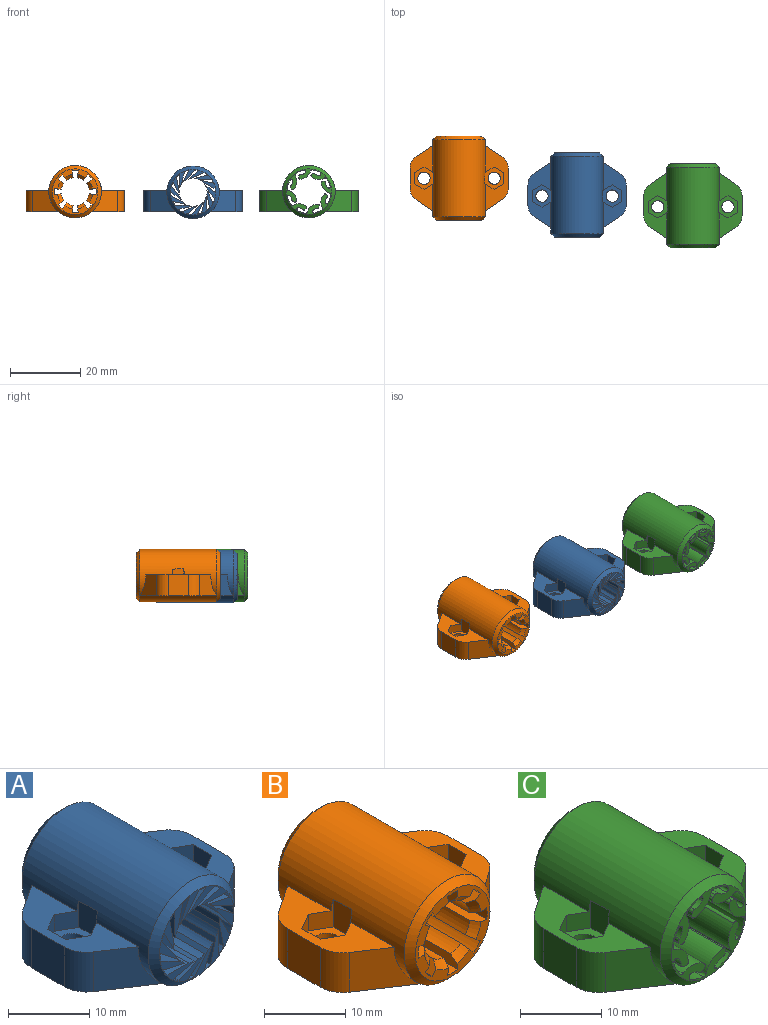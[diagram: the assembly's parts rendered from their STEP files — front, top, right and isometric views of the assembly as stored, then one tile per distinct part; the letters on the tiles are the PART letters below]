
ASSEMBLY  parts=3 mates=2
PART A: 91 faces, bbox 28x24x15 mm
  f0: plane 18.59x6.51mm, normal (0,0,1), area 66.2mm2, adj f1,f2,f4,f5,f6,f7,f82,f83
  f1: cylinder r=7.5mm len=22mm, axis (0,1,0), area 762.8mm2, adj f0,f3,f4,f5,f66,f67,f68,f69
  f2: plane 6x5.69mm, normal (-1,0,0), area 34.2mm2, adj f0,f3,f6,f7
  f3: plane 21.87x9mm, normal (0,0,-1), area 132.4mm2, adj f1,f2,f4,f5,f6,f7,f89
  f4: plane 7.2x6mm, normal (-0.55,-0.83,0), area 38.9mm2, adj f0,f1,f3,f6
  f5: plane 7.2x6mm, normal (-0.55,0.83,0), area 38.9mm2, adj f0,f1,f3,f7
  f6: cylinder r=4mm len=6mm, axis (0,0,-1), area 23.7mm2, adj f0,f2,f3,f4
  f7: cylinder r=4mm len=6mm, axis (0,0,-1), area 23.7mm2, adj f0,f2,f3,f5
  f8: cylinder r=6.35mm len=24mm, axis (0,1,0), area 28.5mm2, adj f9,f63,f64,f65
  f9: plane 24x3.4mm, normal (-0.9,0,-0.44), area 91mm2, adj f8,f10,f64,f65
  f10: cylinder r=4mm len=24mm, axis (0,1,0), area 25.1mm2, adj f9,f11,f64,f65
  f11: plane 24x3.72mm, normal (0.98,0,0.2), area 91mm2, adj f10,f12,f64,f65
  f12: cylinder r=6.35mm len=24mm, axis (0,1,0), area 28.5mm2, adj f11,f13,f64,f65
  f13: plane 24x3.79mm, normal (-1,0,-0.01), area 91mm2, adj f12,f14,f64,f65
  f14: cylinder r=4mm len=24mm, axis (0,1,0), area 25.1mm2, adj f13,f15,f64,f65
  f15: plane 24x3.67mm, normal (0.97,0,-0.25), area 91mm2, adj f14,f16,f64,f65
  f16: cylinder r=6.35mm len=24mm, axis (0,1,0), area 28.5mm2, adj f15,f17,f64,f65
  f17: plane 24x3.44mm, normal (-0.91,0,0.42), area 91mm2, adj f16,f18,f64,f65
  f18: cylinder r=4mm len=24mm, axis (0,1,0), area 25.1mm2, adj f17,f19,f64,f65
  f19: plane 24x2.9mm, normal (0.77,0,-0.64), area 91mm2, adj f18,f20,f64,f65
  f20: cylinder r=6.35mm len=24mm, axis (0,1,0), area 28.5mm2, adj f19,f21,f64,f65
  f21: plane 24x2.94mm, normal (-0.63,0,0.77), area 91mm2, adj f20,f22,f64,f65
  f22: cylinder r=4mm len=24mm, axis (0,1,0), area 25.1mm2, adj f21,f23,f64,f65
  f23: plane 24x3.46mm, normal (0.41,0,-0.91), area 91mm2, adj f22,f24,f64,f65
  f24: cylinder r=6.35mm len=24mm, axis (0,1,0), area 28.5mm2, adj f23,f25,f64,f65
  f25: plane 24x3.69mm, normal (-0.23,0,0.97), area 91mm2, adj f24,f26,f64,f65
  f26: cylinder r=4mm len=24mm, axis (0,1,0), area 25.1mm2, adj f25,f27,f64,f65
  f27: plane 24x3.79mm, normal (-0.03,0,-1), area 91mm2, adj f26,f28,f64,f65
  f28: cylinder r=6.35mm len=24mm, axis (0,1,0), area 28.5mm2, adj f27,f29,f64,f65
  f29: plane 24x3.71mm, normal (0.21,0,0.98), area 91mm2, adj f28,f30,f64,f65
  f30: cylinder r=4mm len=24mm, axis (0,1,0), area 25.1mm2, adj f29,f31,f64,f65
  f31: plane 24x3.37mm, normal (-0.46,0,-0.89), area 91mm2, adj f30,f32,f64,f65
  f32: cylinder r=6.35mm len=24mm, axis (0,1,0), area 28.5mm2, adj f31,f33,f64,f65
  f33: plane 24x2.99mm, normal (0.61,0,0.79), area 91mm2, adj f32,f34,f64,f65
  f34: cylinder r=4mm len=24mm, axis (0,1,0), area 25.1mm2, adj f33,f35,f64,f65
  f35: plane 24x3.02mm, normal (-0.8,0,-0.6), area 91mm2, adj f34,f36,f64,f65
  f36: cylinder r=6.35mm len=24mm, axis (0,1,0), area 28.5mm2, adj f35,f37,f64,f65
  f37: plane 24x3.4mm, normal (0.9,0,0.44), area 91mm2, adj f36,f38,f64,f65
  f38: cylinder r=4mm len=24mm, axis (0,1,0), area 25.1mm2, adj f37,f39,f64,f65
  f39: plane 24x3.72mm, normal (-0.98,0,-0.2), area 91mm2, adj f38,f40,f64,f65
  f40: cylinder r=6.35mm len=24mm, axis (0,1,0), area 28.5mm2, adj f39,f41,f64,f65
  f41: plane 24x3.79mm, normal (1,0,0.01), area 91mm2, adj f40,f42,f64,f65
  f42: cylinder r=4mm len=24mm, axis (0,1,0), area 25.1mm2, adj f41,f43,f64,f65
  f43: plane 24x3.67mm, normal (-0.97,0,0.25), area 91mm2, adj f42,f44,f64,f65
  f44: cylinder r=6.35mm len=24mm, axis (0,1,0), area 28.5mm2, adj f43,f45,f64,f65
  f45: plane 24x3.44mm, normal (0.91,0,-0.42), area 91mm2, adj f44,f46,f64,f65
  f46: cylinder r=4mm len=24mm, axis (0,1,0), area 25.1mm2, adj f45,f47,f64,f65
  f47: plane 24x2.9mm, normal (-0.77,0,0.64), area 91mm2, adj f46,f48,f64,f65
  f48: cylinder r=6.35mm len=24mm, axis (0,1,0), area 28.5mm2, adj f47,f49,f64,f65
  f49: plane 24x2.94mm, normal (0.63,0,-0.77), area 91mm2, adj f48,f50,f64,f65
  f50: cylinder r=4mm len=24mm, axis (0,1,0), area 25.1mm2, adj f49,f51,f64,f65
  f51: plane 24x3.46mm, normal (-0.41,0,0.91), area 91mm2, adj f50,f52,f64,f65
  f52: cylinder r=6.35mm len=24mm, axis (0,1,0), area 28.5mm2, adj f51,f53,f64,f65
  f53: plane 24x3.69mm, normal (0.23,0,-0.97), area 91mm2, adj f52,f54,f64,f65
  f54: cylinder r=4mm len=24mm, axis (0,1,0), area 25.1mm2, adj f53,f55,f64,f65
  f55: plane 24x3.79mm, normal (0.03,0,1), area 91mm2, adj f54,f56,f64,f65
  f56: cylinder r=6.35mm len=24mm, axis (0,1,0), area 28.5mm2, adj f55,f57,f64,f65
  f57: plane 24x3.71mm, normal (-0.21,0,-0.98), area 91mm2, adj f56,f58,f64,f65
  f58: cylinder r=4mm len=24mm, axis (0,1,0), area 25.1mm2, adj f57,f59,f64,f65
  f59: plane 24x3.37mm, normal (0.46,0,0.89), area 91mm2, adj f58,f60,f64,f65
  f60: cylinder r=6.35mm len=24mm, axis (0,1,0), area 28.5mm2, adj f59,f61,f64,f65
  f61: plane 24x2.99mm, normal (-0.61,0,-0.79), area 91mm2, adj f60,f62,f64,f65
  f62: cylinder r=4mm len=24mm, axis (0,1,0), area 25.1mm2, adj f61,f63,f64,f65
  f63: plane 24x3.02mm, normal (0.8,0,0.6), area 91mm2, adj f8,f62,f64,f65
  f64: plane 13x13mm, normal (0,-1,0), area 50.6mm2, adj f8,f9,f10,f11,f12,f13,f14,f15
  f65: plane 13x13mm, normal (0,1,0), area 50.6mm2, adj f8,f9,f10,f11,f12,f13,f14,f15
  f66: cone r=6.5mm half-angle=45deg, axis (0,1,0), area 62.2mm2, adj f1,f64
  f67: cone r=7.5mm half-angle=45deg, axis (0,-1,0), area 62.2mm2, adj f1,f65
  f68: plane 18.59x6.51mm, normal (0,0,1), area 66.2mm2, adj f1,f70,f71,f72,f73,f74,f76,f77
  f69: plane 21.87x9mm, normal (0,0,-1), area 132.4mm2, adj f1,f70,f71,f72,f73,f74,f90
  f70: plane 6x5.69mm, normal (1,0,0), area 34.2mm2, adj f68,f69,f73,f74
  f71: plane 7.2x6mm, normal (0.55,0.83,0), area 38.9mm2, adj f1,f68,f69,f73
  f72: plane 7.2x6mm, normal (0.55,-0.83,0), area 38.9mm2, adj f1,f68,f69,f74
  f73: cylinder r=4mm len=6mm, axis (0,0,1), area 23.7mm2, adj f68,f69,f70,f71
  f74: cylinder r=4mm len=6mm, axis (0,0,1), area 23.7mm2, adj f68,f69,f70,f72
  f75: plane 4.04x3.18mm, normal (1,-0.01,0), area 12.7mm2, adj f1,f76,f77,f81
  f76: plane 4.04x2.74mm, normal (0.5,0.86,0), area 8.2mm2, adj f1,f68,f75,f78,f81
  f77: plane 3.98x2.76mm, normal (0.5,-0.87,0), area 8.2mm2, adj f1,f68,f75,f80,f81
  f78: plane 2.76x2.5mm, normal (-0.5,0.87,0), area 7.9mm2, adj f68,f76,f79,f81
  f79: plane 3.18x2.5mm, normal (-1,0.01,0), area 7.9mm2, adj f68,f78,f80,f81
  f80: plane 2.74x2.5mm, normal (-0.5,-0.86,0), area 7.9mm2, adj f68,f77,f79,f81
  f81: plane 6.35x5.52mm, normal (0,0,1), area 16.6mm2, adj f75,f76,f77,f78,f79,f80,f90
  f82: plane 2.74x2.5mm, normal (0.5,-0.86,0), area 7.9mm2, adj f0,f83,f87,f88
  f83: plane 3.18x2.5mm, normal (1,0.01,0), area 7.9mm2, adj f0,f82,f84,f88
  f84: plane 2.76x2.5mm, normal (0.5,0.87,0), area 7.9mm2, adj f0,f83,f85,f88
  f85: plane 4.04x2.74mm, normal (-0.5,0.86,0), area 8.2mm2, adj f0,f1,f84,f86,f88
  f86: plane 4.04x3.18mm, normal (-1,-0.01,0), area 12.7mm2, adj f1,f85,f87,f88
  f87: plane 3.98x2.76mm, normal (-0.5,-0.87,0), area 8.2mm2, adj f0,f1,f82,f86,f88
  f88: plane 6.35x5.52mm, normal (0,0,1), area 16.6mm2, adj f82,f83,f84,f85,f86,f87,f89
  f89: cylinder r=1.75mm len=3.5mm, axis (0,0,1), area 38.5mm2, adj f3,f88
  f90: cylinder r=1.75mm len=3.5mm, axis (0,0,1), area 38.5mm2, adj f69,f81
PART B: 88 faces, bbox 28x24x15 mm
  f0: plane 18.58x6.5mm, normal (0,0,1), area 66.1mm2, adj f1,f2,f6,f7,f8,f9,f79,f80
  f1: cylinder r=7.5mm len=22mm, axis (0,1,0), area 527.2mm2, adj f0,f6,f7,f45,f46,f63,f68,f69
  f2: plane 6x5.69mm, normal (-1,0,0), area 34.2mm2, adj f0,f3,f8,f9
  f3: plane 22x9.2mm, normal (0,0,-1), area 136.8mm2, adj f2,f4,f5,f6,f7,f8,f9,f10
  f4: plane 0.1x0.08mm, normal (0,-1,0), area 0mm2, adj f3,f6,f45
  f5: plane 0.1x0.08mm, normal (0,1,0), area 0mm2, adj f3,f7,f46
  f6: plane 7.3x6mm, normal (-0.55,-0.83,0), area 39.5mm2, adj f0,f1,f3,f4,f8
  f7: plane 7.3x6mm, normal (-0.55,0.83,0), area 39.5mm2, adj f0,f1,f3,f5,f9
  f8: cylinder r=4mm len=6mm, axis (0,0,-1), area 23.7mm2, adj f0,f2,f3,f6
  f9: cylinder r=4mm len=6mm, axis (0,0,-1), area 23.7mm2, adj f0,f2,f3,f7
  f10: cylinder r=7.5mm len=22mm, axis (0,1,0), area 229.2mm2, adj f3,f45,f46,f64
  f11: plane 24x1.61mm, normal (0.6,0,0.8), area 47mm2, adj f12,f42,f43,f44,f49,f61
  f12: cylinder r=6mm len=24mm, axis (0,1,0), area 42.5mm2, adj f11,f13,f43,f44
  f13: plane 24x1.61mm, normal (-0.8,0,-0.6), area 47mm2, adj f12,f14,f43,f44,f50,f62
  f14: cylinder r=4mm len=22mm, axis (0,1,0), area 43.1mm2, adj f13,f15,f50,f62
  f15: plane 24x1.98mm, normal (0.99,0,0.15), area 47mm2, adj f14,f16,f43,f44,f50,f62
  f16: cylinder r=6mm len=24mm, axis (0,1,0), area 42.5mm2, adj f15,f17,f43,f44
  f17: plane 24x1.98mm, normal (-0.99,0,0.15), area 47mm2, adj f16,f18,f43,f44,f51,f55
  f18: cylinder r=4mm len=22mm, axis (0,1,0), area 43.1mm2, adj f17,f19,f51,f55
  f19: plane 24x1.61mm, normal (0.8,0,-0.6), area 47mm2, adj f18,f20,f43,f44,f51,f55
  f20: cylinder r=6mm len=24mm, axis (0,1,0), area 42.5mm2, adj f19,f21,f43,f44
  f21: plane 24x1.61mm, normal (-0.6,0,0.8), area 47mm2, adj f20,f22,f43,f44,f52,f56
  f22: cylinder r=4mm len=22mm, axis (0,1,0), area 43.1mm2, adj f21,f23,f52,f56
  f23: plane 24x1.98mm, normal (0.15,0,-0.99), area 47mm2, adj f22,f24,f43,f44,f52,f56
  f24: cylinder r=6mm len=24mm, axis (0,1,0), area 42.5mm2, adj f23,f25,f43,f44
  f25: plane 24x1.98mm, normal (0.15,0,0.99), area 47mm2, adj f24,f26,f43,f44,f53,f57
  f26: cylinder r=4mm len=22mm, axis (0,1,0), area 43.1mm2, adj f25,f27,f53,f57
  f27: plane 24x1.61mm, normal (-0.6,0,-0.8), area 47mm2, adj f26,f28,f43,f44,f53,f57
  f28: cylinder r=6mm len=24mm, axis (0,1,0), area 42.5mm2, adj f27,f29,f43,f44
  f29: plane 24x1.61mm, normal (0.8,0,0.6), area 47mm2, adj f28,f30,f43,f44,f54,f58
  f30: cylinder r=4mm len=22mm, axis (0,1,0), area 43.1mm2, adj f29,f31,f54,f58
  f31: plane 24x1.98mm, normal (-0.99,0,-0.15), area 47mm2, adj f30,f32,f43,f44,f54,f58
  f32: cylinder r=6mm len=24mm, axis (0,1,0), area 42.5mm2, adj f31,f33,f43,f44
  f33: plane 24x1.98mm, normal (0.99,0,-0.15), area 47mm2, adj f32,f34,f43,f44,f47,f59
  f34: cylinder r=4mm len=22mm, axis (0,1,0), area 43.1mm2, adj f33,f35,f47,f59
  f35: plane 24x1.61mm, normal (-0.8,0,0.6), area 47mm2, adj f34,f36,f43,f44,f47,f59
  f36: cylinder r=6mm len=24mm, axis (0,1,0), area 42.5mm2, adj f35,f37,f43,f44
  f37: plane 24x1.61mm, normal (0.6,0,-0.8), area 47mm2, adj f36,f38,f43,f44,f48,f60
  f38: cylinder r=4mm len=22mm, axis (0,1,0), area 43.1mm2, adj f37,f39,f48,f60
  f39: plane 24x1.98mm, normal (-0.15,0,0.99), area 47mm2, adj f38,f40,f43,f44,f48,f60
  f40: cylinder r=6mm len=24mm, axis (0,1,0), area 42.5mm2, adj f39,f41,f43,f44
  f41: plane 24x1.98mm, normal (-0.15,0,-0.99), area 47mm2, adj f40,f42,f43,f44,f49,f61
  f42: cylinder r=4mm len=22mm, axis (0,1,0), area 43.1mm2, adj f11,f41,f49,f61
  f43: plane 13x13mm, normal (0,-1,0), area 41.2mm2, adj f11,f12,f13,f15,f16,f17,f19,f20
  f44: plane 13x13mm, normal (0,1,0), area 41.2mm2, adj f11,f12,f13,f15,f16,f17,f19,f20
  f45: cone r=6.5mm half-angle=45deg, axis (0,1,0), area 62.2mm2, adj f1,f4,f10,f43,f66
  f46: cone r=7.5mm half-angle=45deg, axis (0,-1,0), area 62.2mm2, adj f1,f5,f10,f44,f67
  f47: cone r=5mm half-angle=45deg, axis (0,1,0), area 3.1mm2, adj f33,f34,f35,f44
  f48: cone r=5mm half-angle=45deg, axis (0,1,0), area 3.1mm2, adj f37,f38,f39,f44
  f49: cone r=5mm half-angle=45deg, axis (0,1,0), area 3.1mm2, adj f11,f41,f42,f44
  f50: cone r=5mm half-angle=45deg, axis (0,1,0), area 3.1mm2, adj f13,f14,f15,f44
  f51: cone r=5mm half-angle=45deg, axis (0,1,0), area 3.1mm2, adj f17,f18,f19,f44
  f52: cone r=5mm half-angle=45deg, axis (0,1,0), area 3.1mm2, adj f21,f22,f23,f44
  f53: cone r=5mm half-angle=45deg, axis (0,1,0), area 3.1mm2, adj f25,f26,f27,f44
  f54: cone r=5mm half-angle=45deg, axis (0,1,0), area 3.1mm2, adj f29,f30,f31,f44
  f55: cone r=4mm half-angle=45deg, axis (0,-1,0), area 3.1mm2, adj f17,f18,f19,f43
  f56: cone r=4mm half-angle=45deg, axis (0,-1,0), area 3.1mm2, adj f21,f22,f23,f43
  f57: cone r=4mm half-angle=45deg, axis (0,-1,0), area 3.1mm2, adj f25,f26,f27,f43
  f58: cone r=4mm half-angle=45deg, axis (0,-1,0), area 3.1mm2, adj f29,f30,f31,f43
  f59: cone r=4mm half-angle=45deg, axis (0,-1,0), area 3.1mm2, adj f33,f34,f35,f43
  f60: cone r=4mm half-angle=45deg, axis (0,-1,0), area 3.1mm2, adj f37,f38,f39,f43
  f61: cone r=4mm half-angle=45deg, axis (0,-1,0), area 3.1mm2, adj f11,f41,f42,f43
  f62: cone r=4mm half-angle=45deg, axis (0,-1,0), area 3.1mm2, adj f13,f14,f15,f43
  f63: plane 18.58x6.5mm, normal (0,0,1), area 66.1mm2, adj f1,f65,f68,f69,f70,f71,f73,f74
  f64: plane 22x9.2mm, normal (0,0,-1), area 136.8mm2, adj f10,f65,f66,f67,f68,f69,f70,f71
  f65: plane 6x5.69mm, normal (1,0,0), area 34.2mm2, adj f63,f64,f70,f71
  f66: plane 0.1x0.08mm, normal (0,-1,0), area 0mm2, adj f45,f64,f69
  f67: plane 0.1x0.08mm, normal (0,1,0), area 0mm2, adj f46,f64,f68
  f68: plane 7.3x6mm, normal (0.55,0.83,0), area 39.5mm2, adj f1,f63,f64,f67,f70
  f69: plane 7.3x6mm, normal (0.55,-0.83,0), area 39.5mm2, adj f1,f63,f64,f66,f71
  f70: cylinder r=4mm len=6mm, axis (0,0,1), area 23.7mm2, adj f63,f64,f65,f68
  f71: cylinder r=4mm len=6mm, axis (0,0,1), area 23.7mm2, adj f63,f64,f65,f69
  f72: plane 4.22x3.18mm, normal (1,-0.01,0), area 13.3mm2, adj f1,f73,f74,f78
  f73: plane 4.22x2.74mm, normal (0.5,0.86,0), area 8.3mm2, adj f1,f63,f72,f75,f78
  f74: plane 4.15x2.76mm, normal (0.5,-0.87,0), area 8.2mm2, adj f1,f63,f72,f77,f78
  f75: plane 2.76x2.5mm, normal (-0.5,0.87,0), area 7.9mm2, adj f63,f73,f76,f78
  f76: plane 3.18x2.5mm, normal (-1,0.01,0), area 7.9mm2, adj f63,f75,f77,f78
  f77: plane 2.74x2.5mm, normal (-0.5,-0.86,0), area 7.9mm2, adj f63,f74,f76,f78
  f78: plane 6.35x5.52mm, normal (0,0,1), area 16.6mm2, adj f72,f73,f74,f75,f76,f77,f87
  f79: plane 2.74x2.5mm, normal (0.5,-0.86,0), area 7.9mm2, adj f0,f80,f84,f85
  f80: plane 3.18x2.5mm, normal (1,0.01,0), area 7.9mm2, adj f0,f79,f81,f85
  f81: plane 2.76x2.5mm, normal (0.5,0.87,0), area 7.9mm2, adj f0,f80,f82,f85
  f82: plane 4.22x2.74mm, normal (-0.5,0.86,0), area 8.3mm2, adj f0,f1,f81,f83,f85
  f83: plane 4.22x3.18mm, normal (-1,-0.01,0), area 13.3mm2, adj f1,f82,f84,f85
  f84: plane 4.15x2.76mm, normal (-0.5,-0.87,0), area 8.2mm2, adj f0,f1,f79,f83,f85
  f85: plane 6.35x5.52mm, normal (0,0,1), area 16.6mm2, adj f79,f80,f81,f82,f83,f84,f86
  f86: cylinder r=1.75mm len=3.5mm, axis (0,0,1), area 38.5mm2, adj f3,f85
  f87: cylinder r=1.75mm len=3.5mm, axis (0,0,1), area 38.5mm2, adj f64,f78
PART C: 104 faces, bbox 28x24x15 mm
  f0: plane 18.58x6.5mm, normal (0,0,1), area 66.1mm2, adj f1,f2,f6,f7,f8,f9,f95,f96
  f1: cylinder r=7.5mm len=22mm, axis (0,1,0), area 527.2mm2, adj f0,f6,f7,f77,f78,f79,f84,f85
  f2: plane 6x5.69mm, normal (-1,0,0), area 34.2mm2, adj f0,f3,f8,f9
  f3: plane 22x9.2mm, normal (0,0,-1), area 136.8mm2, adj f2,f4,f5,f6,f7,f8,f9,f10
  f4: plane 0.1x0.08mm, normal (0,-1,0), area 0mm2, adj f3,f6,f77
  f5: plane 0.1x0.08mm, normal (0,1,0), area 0mm2, adj f3,f7,f78
  f6: plane 7.3x6mm, normal (-0.55,-0.83,0), area 39.5mm2, adj f0,f1,f3,f4,f8
  f7: plane 7.3x6mm, normal (-0.55,0.83,0), area 39.5mm2, adj f0,f1,f3,f5,f9
  f8: cylinder r=4mm len=6mm, axis (0,0,-1), area 23.7mm2, adj f0,f2,f3,f6
  f9: cylinder r=4mm len=6mm, axis (0,0,-1), area 23.7mm2, adj f0,f2,f3,f7
  f10: cylinder r=7.5mm len=22mm, axis (0,1,0), area 229.2mm2, adj f3,f77,f78,f80
  f11: cylinder r=6.26mm len=24mm, axis (0,1,0), area 60.5mm2, adj f12,f74,f75,f76
  f12: cylinder r=0.4mm len=24mm, axis (0,1,0), area 24.7mm2, adj f11,f13,f75,f76
  f13: cylinder r=1.94mm len=24mm, axis (0,1,0), area 37.1mm2, adj f12,f14,f75,f76
  f14: cylinder r=0.4mm len=24mm, axis (0,1,0), area 13.5mm2, adj f13,f15,f75,f76
  f15: plane 24x0.38mm, normal (-0.59,0,0.81), area 11.2mm2, adj f14,f16,f75,f76
  f16: cylinder r=0.4mm len=24mm, axis (0,1,0), area 16.8mm2, adj f15,f17,f75,f76
  f17: cylinder r=3.19mm len=24mm, axis (0,1,0), area 97.8mm2, adj f16,f18,f75,f76
  f18: cylinder r=0.4mm len=24mm, axis (0,1,0), area 13.9mm2, adj f17,f19,f75,f76
  f19: cylinder r=6.26mm len=24mm, axis (0,1,0), area 60.5mm2, adj f18,f20,f75,f76
  f20: cylinder r=0.4mm len=24mm, axis (0,1,0), area 24.7mm2, adj f19,f21,f75,f76
  f21: cylinder r=1.94mm len=24mm, axis (0,1,0), area 37.1mm2, adj f20,f22,f75,f76
  f22: cylinder r=0.4mm len=24mm, axis (0,1,0), area 13.5mm2, adj f21,f23,f75,f76
  f23: plane 24x0.46mm, normal (0.16,0,0.99), area 11.2mm2, adj f22,f24,f75,f76
  f24: cylinder r=0.4mm len=24mm, axis (0,1,0), area 16.8mm2, adj f23,f25,f75,f76
  f25: cylinder r=3.19mm len=24mm, axis (0,1,0), area 97.8mm2, adj f24,f26,f75,f76
  f26: cylinder r=0.4mm len=24mm, axis (0,1,0), area 13.9mm2, adj f25,f27,f75,f76
  f27: cylinder r=6.26mm len=24mm, axis (0,1,0), area 60.5mm2, adj f26,f28,f75,f76
  f28: cylinder r=0.4mm len=24mm, axis (0,1,0), area 24.7mm2, adj f27,f29,f75,f76
  f29: cylinder r=1.94mm len=24mm, axis (0,1,0), area 37.1mm2, adj f28,f30,f75,f76
  f30: cylinder r=0.4mm len=24mm, axis (0,1,0), area 13.5mm2, adj f29,f31,f75,f76
  f31: plane 24x0.38mm, normal (0.81,0,0.59), area 11.2mm2, adj f30,f32,f75,f76
  f32: cylinder r=0.4mm len=24mm, axis (0,1,0), area 16.8mm2, adj f31,f33,f75,f76
  f33: cylinder r=3.19mm len=24mm, axis (0,1,0), area 97.8mm2, adj f32,f34,f75,f76
  f34: cylinder r=0.4mm len=24mm, axis (0,1,0), area 13.9mm2, adj f33,f35,f75,f76
  f35: cylinder r=6.26mm len=24mm, axis (0,1,0), area 60.5mm2, adj f34,f36,f75,f76
  f36: cylinder r=0.4mm len=24mm, axis (0,1,0), area 24.7mm2, adj f35,f37,f75,f76
  f37: cylinder r=1.94mm len=24mm, axis (0,1,0), area 37.1mm2, adj f36,f38,f75,f76
  f38: cylinder r=0.4mm len=24mm, axis (0,1,0), area 13.5mm2, adj f37,f39,f75,f76
  f39: plane 24x0.46mm, normal (0.99,0,-0.16), area 11.2mm2, adj f38,f40,f75,f76
  f40: cylinder r=0.4mm len=24mm, axis (0,1,0), area 16.8mm2, adj f39,f41,f75,f76
  f41: cylinder r=3.19mm len=24mm, axis (0,1,0), area 97.8mm2, adj f40,f42,f75,f76
  f42: cylinder r=0.4mm len=24mm, axis (0,1,0), area 13.9mm2, adj f41,f43,f75,f76
  f43: cylinder r=6.26mm len=24mm, axis (0,1,0), area 60.5mm2, adj f42,f44,f75,f76
  f44: cylinder r=0.4mm len=24mm, axis (0,1,0), area 24.7mm2, adj f43,f45,f75,f76
  f45: cylinder r=1.94mm len=24mm, axis (0,1,0), area 37.1mm2, adj f44,f46,f75,f76
  f46: cylinder r=0.4mm len=24mm, axis (0,1,0), area 13.5mm2, adj f45,f47,f75,f76
  f47: plane 24x0.38mm, normal (0.59,0,-0.81), area 11.2mm2, adj f46,f48,f75,f76
  f48: cylinder r=0.4mm len=24mm, axis (0,1,0), area 16.8mm2, adj f47,f49,f75,f76
  f49: cylinder r=3.19mm len=24mm, axis (0,1,0), area 97.8mm2, adj f48,f50,f75,f76
  f50: cylinder r=0.4mm len=24mm, axis (0,1,0), area 13.9mm2, adj f49,f51,f75,f76
  f51: cylinder r=6.26mm len=24mm, axis (0,1,0), area 60.5mm2, adj f50,f52,f75,f76
  f52: cylinder r=0.4mm len=24mm, axis (0,1,0), area 24.7mm2, adj f51,f53,f75,f76
  f53: cylinder r=1.94mm len=24mm, axis (0,1,0), area 37.1mm2, adj f52,f54,f75,f76
  f54: cylinder r=0.4mm len=24mm, axis (0,1,0), area 13.5mm2, adj f53,f55,f75,f76
  f55: plane 24x0.46mm, normal (-0.16,0,-0.99), area 11.2mm2, adj f54,f56,f75,f76
  f56: cylinder r=0.4mm len=24mm, axis (0,1,0), area 16.8mm2, adj f55,f57,f75,f76
  f57: cylinder r=3.19mm len=24mm, axis (0,1,0), area 97.8mm2, adj f56,f58,f75,f76
  f58: cylinder r=0.4mm len=24mm, axis (0,1,0), area 13.9mm2, adj f57,f59,f75,f76
  f59: cylinder r=6.26mm len=24mm, axis (0,1,0), area 60.5mm2, adj f58,f60,f75,f76
  f60: cylinder r=0.4mm len=24mm, axis (0,1,0), area 24.7mm2, adj f59,f61,f75,f76
  f61: cylinder r=1.94mm len=24mm, axis (0,1,0), area 37.1mm2, adj f60,f62,f75,f76
  f62: cylinder r=0.4mm len=24mm, axis (0,1,0), area 13.5mm2, adj f61,f63,f75,f76
  f63: plane 24x0.38mm, normal (-0.81,0,-0.59), area 11.2mm2, adj f62,f64,f75,f76
  f64: cylinder r=0.4mm len=24mm, axis (0,1,0), area 16.8mm2, adj f63,f65,f75,f76
  f65: cylinder r=3.19mm len=24mm, axis (0,1,0), area 97.8mm2, adj f64,f66,f75,f76
  f66: cylinder r=0.4mm len=24mm, axis (0,1,0), area 13.9mm2, adj f65,f67,f75,f76
  f67: cylinder r=6.26mm len=24mm, axis (0,1,0), area 60.5mm2, adj f66,f68,f75,f76
  f68: cylinder r=0.4mm len=24mm, axis (0,1,0), area 24.7mm2, adj f67,f69,f75,f76
  f69: cylinder r=1.94mm len=24mm, axis (0,1,0), area 37.1mm2, adj f68,f70,f75,f76
  f70: cylinder r=0.4mm len=24mm, axis (0,1,0), area 13.5mm2, adj f69,f71,f75,f76
  f71: plane 24x0.46mm, normal (-0.99,0,0.16), area 11.2mm2, adj f70,f72,f75,f76
  f72: cylinder r=0.4mm len=24mm, axis (0,1,0), area 16.8mm2, adj f71,f73,f75,f76
  f73: cylinder r=3.19mm len=24mm, axis (0,1,0), area 97.8mm2, adj f72,f74,f75,f76
  f74: cylinder r=0.4mm len=24mm, axis (0,1,0), area 13.9mm2, adj f11,f73,f75,f76
  f75: plane 13x13mm, normal (0,-1,0), area 47.7mm2, adj f11,f12,f13,f14,f15,f16,f17,f18
  f76: plane 13x13mm, normal (0,1,0), area 47.7mm2, adj f11,f12,f13,f14,f15,f16,f17,f18
  f77: cone r=6.5mm half-angle=45deg, axis (0,1,0), area 62.2mm2, adj f1,f4,f10,f75,f82
  f78: cone r=7.5mm half-angle=45deg, axis (0,-1,0), area 62.2mm2, adj f1,f5,f10,f76,f83
  f79: plane 18.58x6.5mm, normal (0,0,1), area 66.1mm2, adj f1,f81,f84,f85,f86,f87,f89,f90
  f80: plane 22x9.2mm, normal (0,0,-1), area 136.8mm2, adj f10,f81,f82,f83,f84,f85,f86,f87
  f81: plane 6x5.69mm, normal (1,0,0), area 34.2mm2, adj f79,f80,f86,f87
  f82: plane 0.1x0.08mm, normal (0,-1,0), area 0mm2, adj f77,f80,f85
  f83: plane 0.1x0.08mm, normal (0,1,0), area 0mm2, adj f78,f80,f84
  f84: plane 7.3x6mm, normal (0.55,0.83,0), area 39.5mm2, adj f1,f79,f80,f83,f86
  f85: plane 7.3x6mm, normal (0.55,-0.83,0), area 39.5mm2, adj f1,f79,f80,f82,f87
  f86: cylinder r=4mm len=6mm, axis (0,0,1), area 23.7mm2, adj f79,f80,f81,f84
  f87: cylinder r=4mm len=6mm, axis (0,0,1), area 23.7mm2, adj f79,f80,f81,f85
  f88: plane 4.22x3.18mm, normal (1,-0.01,0), area 13.3mm2, adj f1,f89,f90,f94
  f89: plane 4.22x2.74mm, normal (0.5,0.86,0), area 8.3mm2, adj f1,f79,f88,f91,f94
  f90: plane 4.15x2.76mm, normal (0.5,-0.87,0), area 8.2mm2, adj f1,f79,f88,f93,f94
  f91: plane 2.76x2.5mm, normal (-0.5,0.87,0), area 7.9mm2, adj f79,f89,f92,f94
  f92: plane 3.18x2.5mm, normal (-1,0.01,0), area 7.9mm2, adj f79,f91,f93,f94
  f93: plane 2.74x2.5mm, normal (-0.5,-0.86,0), area 7.9mm2, adj f79,f90,f92,f94
  f94: plane 6.35x5.52mm, normal (0,0,1), area 16.6mm2, adj f88,f89,f90,f91,f92,f93,f103
  f95: plane 2.74x2.5mm, normal (0.5,-0.86,0), area 7.9mm2, adj f0,f96,f100,f101
  f96: plane 3.18x2.5mm, normal (1,0.01,0), area 7.9mm2, adj f0,f95,f97,f101
  f97: plane 2.76x2.5mm, normal (0.5,0.87,0), area 7.9mm2, adj f0,f96,f98,f101
  f98: plane 4.22x2.74mm, normal (-0.5,0.86,0), area 8.3mm2, adj f0,f1,f97,f99,f101
  f99: plane 4.22x3.18mm, normal (-1,-0.01,0), area 13.3mm2, adj f1,f98,f100,f101
  f100: plane 4.15x2.76mm, normal (-0.5,-0.87,0), area 8.2mm2, adj f0,f1,f95,f99,f101
  f101: plane 6.35x5.52mm, normal (0,0,1), area 16.6mm2, adj f95,f96,f97,f98,f99,f100,f102
  f102: cylinder r=1.75mm len=3.5mm, axis (0,0,1), area 38.5mm2, adj f3,f101
  f103: cylinder r=1.75mm len=3.5mm, axis (0,0,1), area 38.5mm2, adj f80,f94
PLACE A t=(13.23,-6.87,-69.44)mm
PLACE B t=(-20.38,-2.07,-75.03)mm
PLACE C t=(46.24,-9.93,-69.27)mm
MATE planar A.f74 <-> C.f3  axis (0,0,-1) through (23.23,-9.71,-75.03)mm
MATE planar B.f64 <-> A.f3  axis (0,0,-1) through (-11.83,-10.67,-75.03)mm
